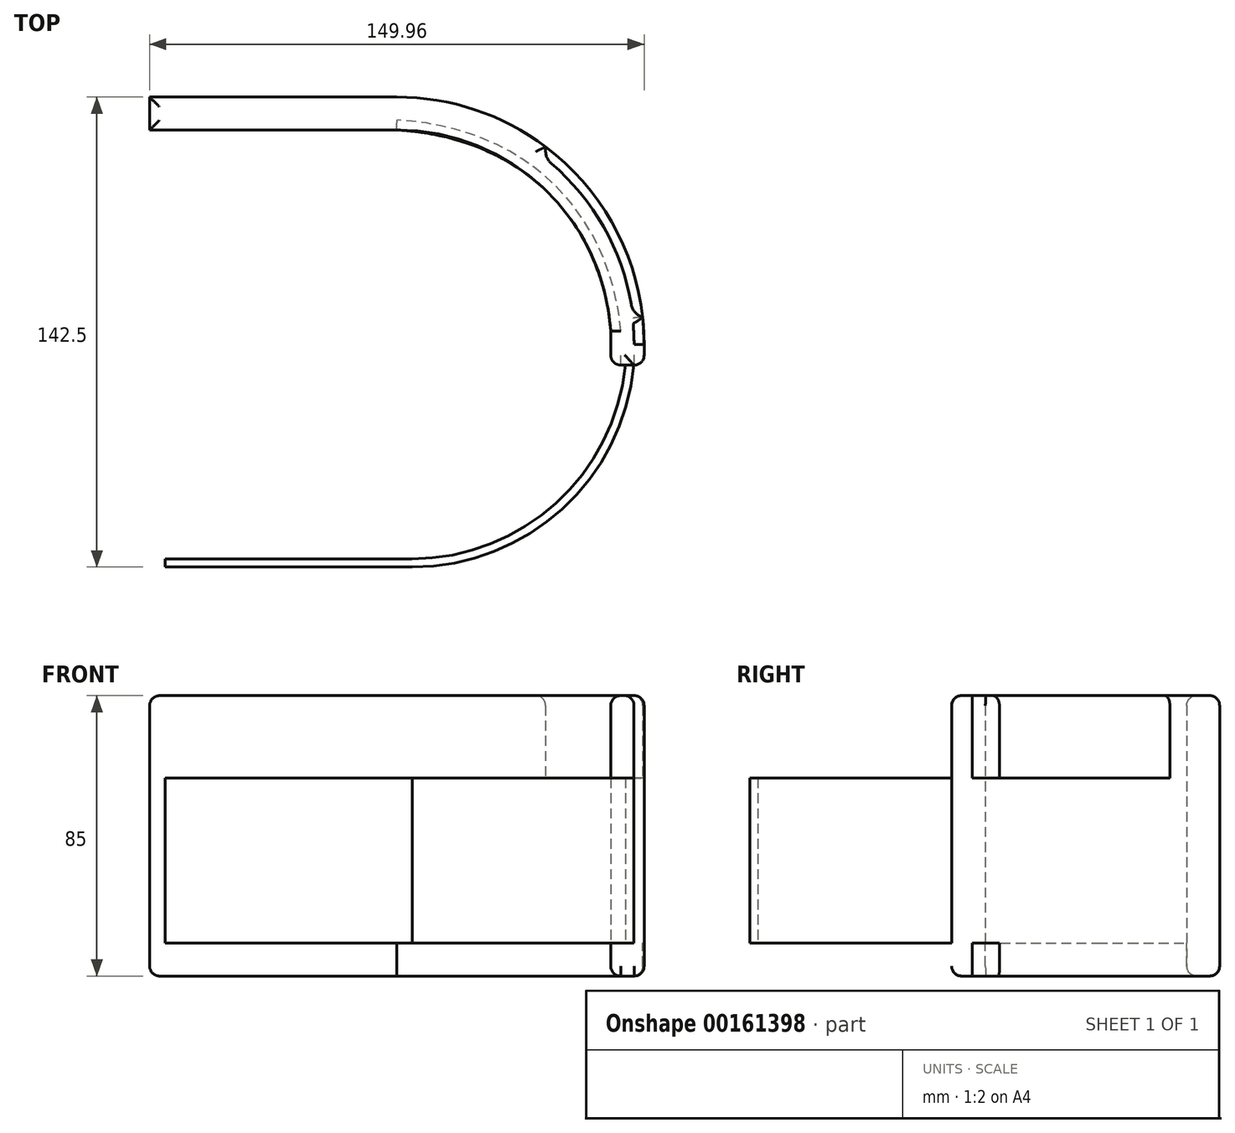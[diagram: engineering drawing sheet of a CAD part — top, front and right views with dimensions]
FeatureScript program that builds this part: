
annotation { "Feature Type Name" : "Feature", "Feature Type Description" : "" }
export const myFeature = defineFeature(function(context is Context, id is Id, definition is map)
    precondition{}
    {
        {
            var Q0;
            Q0=qCreatedBy(makeId("Top.planeOp"),FACE);
            var sketch = newSketch(context, id + "F0", { "sketchPlane" : qUnion([Q0])});
            skLineSegment(sketch, "E0.left", {"start": v(0, 55) * mm, "end": v(0, 54.93) * mm});
            skLineSegment(sketch, "E0.right", {"start": v(-74.96, 75) * mm, "end": v(-74.96, 65) * mm});
            skLineSegment(sketch, "E1.bottom", {"start": v(0, -62.5) * mm, "end": v(0, -62.5) * mm});
            skLineSegment(sketch, "E1.top", {"start": v(0, -65) * mm, "end": v(0, -65) * mm});
            skArc(sketch, "E2", {"start": v(4.58, -65.02) * mm, "mid": v(48.27, -48.15) * mm, "end": v(69.27, -6.28) * mm});
            skArc(sketch, "E3", {"start": v(4.7, -67.5) * mm, "mid": v(50.16, -49.9) * mm, "end": v(71.9, -6.26) * mm});
            skLineSegment(sketch, "E4.top", {"start": v(0, -67.5) * mm, "end": v(0, -67.5) * mm});
            skLineSegment(sketch, "E4.left", {"start": v(4.7, -67.45) * mm, "end": v(4.7, -67.5) * mm});
            skLineSegment(sketch, "E4.right", {"start": v(4.7, -67.45) * mm, "end": v(4.7, -67.5) * mm});
            skLineSegment(sketch, "E5.bottom", {"start": v(-44.95, -65) * mm, "end": v(-70.26, -65) * mm});
            skLineSegment(sketch, "E5.top", {"start": v(-44.95, -67.45) * mm, "end": v(-70.26, -67.45) * mm});
            skLineSegment(sketch, "E5.right", {"start": v(-70.26, -65) * mm, "end": v(-70.26, -67.45) * mm});
            skPoint(sketch, "E6.orphan", {"position": v(0, 75) * mm});
            skPoint(sketch, "E7.firstSnap0", {"position": v(73.69, -6.26) * mm});
            skLineSegment(sketch, "E7.left", {"start": v(64.88, -6.28) * mm, "end": v(64.88, 4) * mm});
            skLineSegment(sketch, "E7.right", {"start": v(75, -6.26) * mm, "end": v(75, 0) * mm});
            skPoint(sketch, "E8.trimOffspring.end.orphan", {"position": v(72.38, -6.26) * mm});
            skLineSegment(sketch, "E9", {"start": v(-74.96, 75) * mm, "end": v(0, 75) * mm});
            skPoint(sketch, "E10.visualSharp", {"position": v(0, 65) * mm});
            skLineSegment(sketch, "E11", {"start": v(64.88, -6.28) * mm, "end": v(69.27, -6.28) * mm});
            skLineSegment(sketch, "E12", {"start": v(71.9, -6.26) * mm, "end": v(75, -6.26) * mm});
            skLineSegment(sketch, "E13", {"start": v(-74.96, 65) * mm, "end": v(0, 65) * mm});
            skArc(sketch, "E14", {"start": v(64.88, 4) * mm, "mid": v(44.53, 47.35) * mm, "end": v(0, 65) * mm});
            skArc(sketch, "E15", {"start": v(75, 0) * mm, "mid": v(53.03, 53.03) * mm, "end": v(0, 75) * mm});
            skPoint(sketch, "E16.top.end.orphan", {"position": v(-44.95, -67.45) * mm});
            skLineSegment(sketch, "E17", {"start": v(-44.95, -65) * mm, "end": v(4.58, -65.02) * mm});
            skLineSegment(sketch, "E18", {"start": v(-44.95, -67.45) * mm, "end": v(4.7, -67.45) * mm});
            skSolve(sketch);
        }
        {
            var Q0;
            Q0 = qSketchRegion(id + "F0", true);
            extrude(context, id + "F1", {"entities" : qUnion([Q0]), "depth" : 50 * mm});
        }
        {
            var Q0;
            Q0=makeQuery(id+"F1.opExtrude","CAP_FACE",FACE,{"disambiguationData":[OSD([sQuery(id+"F0.wireOp",EDGE,"E0.left"),sQuery(id+"F0.wireOp",EDGE,"l4drkFqr-Ext1-0wu3-TS6g-RUhartOmlGj0.bottom"),sQuery(id+"F0.wireOp",EDGE,"l4drkFqr-Ext1-0wu3-TS6g-RUhartOmlGj0.top"),sQuery(id+"F0.wireOp",EDGE,"l4drkFqr-Ext1-0wu3-TS6g-RUhartOmlGj0.left"),sQuery(id+"F0.wireOp",EDGE,"nfyiku83-vluC-BbDP-Zb0F-wST9Rz1iPsC2"),sQuery(id+"F0.wireOp",EDGE,"4fa4322b-fb09-4e2b-9562-7aa5feb7b988.trimOffspring"),sQuery(id+"F0.wireOp",EDGE,"euxQbjAW-CUkM-jL5x-psGC-qHoEu5hEKwZS.bottom"),sQuery(id+"F0.wireOp",EDGE,"euxQbjAW-CUkM-jL5x-psGC-qHoEu5hEKwZS.top"),sQuery(id+"F0.wireOp",EDGE,"euxQbjAW-CUkM-jL5x-psGC-qHoEu5hEKwZS.left"),sQuery(id+"F0.wireOp",EDGE,"euxQbjAW-CUkM-jL5x-psGC-qHoEu5hEKwZS.right"),sQuery(id+"F0.wireOp",EDGE,"E2"),sQuery(id+"F0.wireOp",EDGE,"E3"),sQuery(id+"F0.wireOp",EDGE,"E4.right"),sQuery(id+"F0.wireOp",EDGE,"E16.bottom"),sQuery(id+"F0.wireOp",EDGE,"E16.top"),sQuery(id+"F0.wireOp",EDGE,"E5.bottom"),sQuery(id+"F0.wireOp",EDGE,"E5.top"),sQuery(id+"F0.wireOp",EDGE,"E5.right"),sQuery(id+"F0.wireOp",EDGE,"ff1a45de-c511-4c4a-a1af-e9bdcd5b46a6.trimOffspring")])],"isStart":false});
            var sketch = newSketch(context, id + "F2", { "sketchPlane" : qUnion([Q0])});
            skLineSegment(sketch, "E19.bottom", {"start": v(-5.44, 75) * mm, "end": v(0, 75) * mm});
            skLineSegment(sketch, "E19.left", {"start": v(-74.96, 75) * mm, "end": v(-74.96, 65) * mm});
            skLineSegment(sketch, "E20.top", {"start": v(71.66, 8.23) * mm, "end": v(74.55, 8.23) * mm});
            skArc(sketch, "E21", {"start": v(64.88, 4) * mm, "mid": v(44.92, 46.98) * mm, "end": v(1.1, 65) * mm});
            skArc(sketch, "E22", {"start": v(71.66, 8.23) * mm, "mid": v(63.14, 34.88) * mm, "end": v(45.11, 56.28) * mm});
            skLineSegment(sketch, "E23", {"start": v(45.11, 56.28) * mm, "end": v(45.11, 59.92) * mm});
            skArc(sketch, "E24", {"start": v(45.15, 60.13) * mm, "mid": v(21.2, 72.15) * mm, "end": v(-5.44, 75) * mm});
            skLineSegment(sketch, "E25", {"start": v(-74.96, 65) * mm, "end": v(1.1, 65) * mm});
            skLineSegment(sketch, "E26", {"start": v(75, -6.26) * mm, "end": v(64.88, -6.28) * mm});
            skLineSegment(sketch, "E27", {"start": v(64.88, -6.28) * mm, "end": v(64.88, 4) * mm});
            skLineSegment(sketch, "E28", {"start": v(75, -6.26) * mm, "end": v(75, 0) * mm});
            skFitSpline(sketch, "E29", {"points": [v(74.55, 8.23) * mm, v(75, 0) * mm], "startDerivative": vector(0.75, -8.15) * mm, "endDerivative": vector(0.45, -8.23) * mm});
            skLineSegment(sketch, "E30", {"start": v(-74.96, 75) * mm, "end": v(-5.44, 75) * mm});
            skSolve(sketch);
        }
        {
            var Q0;
            Q0 = qSketchRegion(id + "F2", true);
            var Q1;
            {var subQ13=sQuery(id+"F2.wireOp",EDGE,"E19.left");Q1=makeQuery(id+"F2.imprint","IMPRINT",FACE,{"disambiguationData":[TD([[makeQuery(id+"F2.imprint","IMPRINT",EDGE,{"derivedFrom":subQ13}),1.0]])]});}
            extrude(context, id + "F3", {"entities" : qUnion([Q0, Q1]), "operationType" : NewBodyOperationType.ADD, "depth" : 25 * mm});
        }
        {
            var Q0;
            Q0=makeQuery(id+"F1.opExtrude","CAP_FACE",FACE,{"disambiguationData":[OSD([sQuery(id+"F0.wireOp",EDGE,"E0.left"),sQuery(id+"F0.wireOp",EDGE,"l4drkFqr-Ext1-0wu3-TS6g-RUhartOmlGj0.bottom"),sQuery(id+"F0.wireOp",EDGE,"l4drkFqr-Ext1-0wu3-TS6g-RUhartOmlGj0.top"),sQuery(id+"F0.wireOp",EDGE,"l4drkFqr-Ext1-0wu3-TS6g-RUhartOmlGj0.left"),sQuery(id+"F0.wireOp",EDGE,"nfyiku83-vluC-BbDP-Zb0F-wST9Rz1iPsC2"),sQuery(id+"F0.wireOp",EDGE,"4fa4322b-fb09-4e2b-9562-7aa5feb7b988.trimOffspring"),sQuery(id+"F0.wireOp",EDGE,"euxQbjAW-CUkM-jL5x-psGC-qHoEu5hEKwZS.bottom"),sQuery(id+"F0.wireOp",EDGE,"euxQbjAW-CUkM-jL5x-psGC-qHoEu5hEKwZS.top"),sQuery(id+"F0.wireOp",EDGE,"euxQbjAW-CUkM-jL5x-psGC-qHoEu5hEKwZS.left"),sQuery(id+"F0.wireOp",EDGE,"euxQbjAW-CUkM-jL5x-psGC-qHoEu5hEKwZS.right"),sQuery(id+"F0.wireOp",EDGE,"E2"),sQuery(id+"F0.wireOp",EDGE,"E3"),sQuery(id+"F0.wireOp",EDGE,"E4.right"),sQuery(id+"F0.wireOp",EDGE,"E16.bottom"),sQuery(id+"F0.wireOp",EDGE,"E16.top"),sQuery(id+"F0.wireOp",EDGE,"E5.bottom"),sQuery(id+"F0.wireOp",EDGE,"E5.top"),sQuery(id+"F0.wireOp",EDGE,"E5.right"),sQuery(id+"F0.wireOp",EDGE,"ff1a45de-c511-4c4a-a1af-e9bdcd5b46a6.trimOffspring")])],"isStart":true});
            var sketch = newSketch(context, id + "F4", { "sketchPlane" : qUnion([Q0])});
            skArc(sketch, "E31", {"start": v(0, -75) * mm, "mid": v(50.03, -55.87) * mm, "end": v(74.55, -8.24) * mm});
            skLineSegment(sketch, "E32.top", {"start": v(-74.96, -75) * mm, "end": v(0, -75) * mm});
            skPoint(sketch, "E33.orphan", {"position": v(44.53, -47.35) * mm});
            skFitSpline(sketch, "E34", {"points": [v(0, -65) * mm, v(44.53, -47.35) * mm, v(64.88, -4) * mm], "startDerivative": vector(103.26, 5.34) * mm, "endDerivative": vector(8.06, 102.97) * mm});
            skLineSegment(sketch, "E35", {"start": v(-74.96, -75) * mm, "end": v(-74.96, -65) * mm});
            skLineSegment(sketch, "E36", {"start": v(-74.96, -65) * mm, "end": v(0, -65) * mm});
            skLineSegment(sketch, "E37", {"start": v(64.88, 6.28) * mm, "end": v(75, 6.26) * mm});
            skLineSegment(sketch, "E38", {"start": v(75, 6.26) * mm, "end": v(75, 0) * mm});
            skLineSegment(sketch, "E39", {"start": v(75, 0) * mm, "end": v(74.55, -8.24) * mm});
            skLineSegment(sketch, "E40", {"start": v(64.88, 6.28) * mm, "end": v(64.88, -4) * mm});
            skSolve(sketch);
        }
        {
            var Q0;
            Q0 = qSketchRegion(id + "F4", true);
            extrude(context, id + "F5", {"entities" : qUnion([Q0]), "operationType" : NewBodyOperationType.ADD, "depth" : 10 * mm});
        }
        {
            var Q0;
            Q0=makeQuery(id+"F3.opExtrude","SWEPT_EDGE",EDGE,{"disambiguationData":[OSD([sQuery(id+"F2.wireOp",EDGE,"E20.top"),sQuery(id+"F2.wireOp",EDGE,"E22")])]});
            fillet(context, id + "F6", {"entities" : qUnion([Q0]), "radius" : 5 * mm, "tangentPropagation" : true, "allowEdgeOverflow" : false});
        }
        {
            var Q0;
            Q0=makeQuery(id+"F3.opExtrude","SWEPT_EDGE",EDGE,{"disambiguationData":[OSD([sQuery(id+"F2.wireOp",EDGE,"E22"),sQuery(id+"F2.wireOp",EDGE,"E23")])]});
            fillet(context, id + "F7", {"entities" : qUnion([Q0]), "radius" : 5 * mm, "tangentPropagation" : true, "allowEdgeOverflow" : false});
        }
        {
            var Q0;
            {var subQ0=sQuery(id+"F0.wireOp",EDGE,"E12");Q0=makeQuery(id+"F3.boolean.opBoolean","MERGE",EDGE,{"derivedFrom":[makeQuery(id+"F1.opExtrude","SWEPT_EDGE",EDGE,{"disambiguationData":[OSD([sQuery(id+"F0.wireOp",EDGE,"E7.right"),subQ0])]}),makeQuery(id+"F3.opExtrude","SWEPT_EDGE",EDGE,{"disambiguationData":[OSD([subQ0,sQuery(id+"F2.wireOp",EDGE,"E26"),sQuery(id+"F2.wireOp",EDGE,"E28")])]})]});}
            var Q1;
            Q1=makeQuery(id+"F3.opExtrude","SWEPT_EDGE",EDGE,{"disambiguationData":[OSD([sQuery(id+"F0.wireOp",EDGE,"E11"),sQuery(id+"F2.wireOp",EDGE,"E26"),sQuery(id+"F2.wireOp",EDGE,"E27")])]});
            var Q2;
            Q2=makeQuery(id+"F5.opExtrude","SWEPT_EDGE",EDGE,{"disambiguationData":[OSD([sQuery(id+"F0.wireOp",EDGE,"E12"),sQuery(id+"F4.wireOp",EDGE,"E37"),sQuery(id+"F4.wireOp",EDGE,"E38")])]});
            var Q3;
            Q3=makeQuery(id+"F5.opExtrude","SWEPT_EDGE",EDGE,{"disambiguationData":[OSD([sQuery(id+"F0.wireOp",EDGE,"E11"),sQuery(id+"F4.wireOp",EDGE,"E37"),sQuery(id+"F4.wireOp",EDGE,"E40")])]});
            var Q4;
            Q4=makeQuery(id+"F1.opExtrude","SWEPT_EDGE",EDGE,{"disambiguationData":[OSD([sQuery(id+"F0.wireOp",EDGE,"E7.left"),sQuery(id+"F0.wireOp",EDGE,"E11")])]});
            fillet(context, id + "F8", {"entities" : qUnion([Q0, Q1, Q2, Q3, Q4]), "radius" : 3 * mm, "tangentPropagation" : true, "allowEdgeOverflow" : false});
        }
        {
            var Q0;
            Q0=makeQuery(id+"F5.opExtrude","CAP_FACE",FACE,{"disambiguationData":[OSD([sQuery(id+"F4.wireOp",EDGE,"E31"),sQuery(id+"F4.wireOp",EDGE,"E32.top"),sQuery(id+"F4.wireOp",EDGE,"E34"),sQuery(id+"F4.wireOp",EDGE,"E35"),sQuery(id+"F4.wireOp",EDGE,"E36"),sQuery(id+"F4.wireOp",EDGE,"E37"),sQuery(id+"F4.wireOp",EDGE,"E38"),sQuery(id+"F4.wireOp",EDGE,"E39"),sQuery(id+"F4.wireOp",EDGE,"E40")])],"isStart":false});
            fillet(context, id + "F9", {"entities" : qUnion([Q0]), "radius" : 3 * mm, "tangentPropagation" : true, "allowEdgeOverflow" : false});
        }
        {
            var Q0;
            Q0=makeQuery(id+"F3.opExtrude","CAP_FACE",FACE,{"disambiguationData":[OSD([sQuery(id+"F0.wireOp",EDGE,"E3"),sQuery(id+"F0.wireOp",EDGE,"E12"),sQuery(id+"F0.wireOp",EDGE,"E13"),sQuery(id+"F0.wireOp",EDGE,"E14"),sQuery(id+"F0.wireOp",EDGE,"E15"),sQuery(id+"F2.wireOp",EDGE,"E19.bottom"),sQuery(id+"F2.wireOp",EDGE,"E19.left"),sQuery(id+"F2.wireOp",EDGE,"E20.top"),sQuery(id+"F2.wireOp",EDGE,"E21"),sQuery(id+"F2.wireOp",EDGE,"E22"),sQuery(id+"F2.wireOp",EDGE,"E23"),sQuery(id+"F2.wireOp",EDGE,"E26"),sQuery(id+"F2.wireOp",EDGE,"E27"),sQuery(id+"F2.wireOp",EDGE,"E28"),sQuery(id+"F2.wireOp",EDGE,"E29"),sQuery(id+"F2.wireOp",EDGE,"E30")])],"isStart":false});
            fillet(context, id + "F10", {"entities" : qUnion([Q0]), "radius" : 3 * mm, "tangentPropagation" : true, "allowEdgeOverflow" : false});
        }
    });
